# Revit family: PRD_FrankeWS_TmblrHldrs_FIRMUSTumblerHolder_FIRX006HP
name_source: partatom
category: Specialty Equipment
revit_build: Autodesk Revit 2018 (Build: 20190510_1515(x64)
units: mm (PartAtom-declared; Revit-internal decimal feet)

## family parameters
Cut with Voids When Loaded = No
Host = Face
OmniClass Number = 23.40.20.21
OmniClass Title = Toilet and Bath Specialties
Part Type = Normal
Room Calculation Point = No
Round Connector Dimension = Use Diameter
Shared = No

## types (1)
- FIRX006HP
    AssetType = Fixed
    BIMObjectName = PRD_AR_TumblerHolders_FIRMUSTumblerHolder_FIRX006HP
    Category = Pr_40_20_76_92, Tumbler holders
    CupMaterial = PRD_AR_FrostedGlass
    Default Elevation = 800 mm  [stored 2.62467 ft]
    Description = Tumbler holder for wall mounting, 304 stainless steel, glass cup, round covers with drilled hole on bottom for fixation, inclusive stainless steel screws and dowels.
    DurationUnit = year
    Features = stainless steel, surface high polished
    Finish = high polished
    GrossWeight = 0.40 kg
    HolderMaterial = PRD_AR_StainlessSteel_HighPolished
    IfcExportAs = IfcFurnitureType
    IfcExportType = USERDEFINED
    IntegralAccessories = incl. stainless steel screws and dowels
    IsBuiltIn = TRUE
    MainColor = stainless steel
    Manufacturer = KWC Group AG
    ManufacturerName = KWC Group AG
    ManufacturerURL = www.kwc.com
    Material = stainless steel
    MaterialCode = 1.4301
    Model = FIRX006HP
    ModelNumber = 2000106275
    ModelReference = FIRX006HP
    NBSDescription = Tumbler holders
    NBSReference = 45-35-72/376
    Name = Tumbler Holder FIRX006HP
    NetWeight = 0.36 kg
    NominalDepth = 105 mm  [stored 0.344488 ft]
    NominalHeight = 103 mm  [stored 0.337927 ft]
    NominalWidth = 70 mm  [stored 0.229659 ft]
    ProductInformation = https://pim.kwc.com
    Size = 70 x 103 x 105 mm
    Style = Tumbler holder
    TypeOfFixing = Screw
    TypeOfMounting = Wall mounting
    URL = www.kwc.com
    Uniclass2015Code = Pr_40_20_76_92
    Uniclass2015Title = Tumbler holders
    Uniclass2015Version = Products v1.17
    Version = 1
    WarrantyDurationUnit = year

note: [stored X ft] marks values corroborated as IEEE doubles in the binary element streams (Revit-internal decimal feet)

## geometry (parser evidence)
native form markers: Sweep x1
no freeform markers — native parametric forms only
